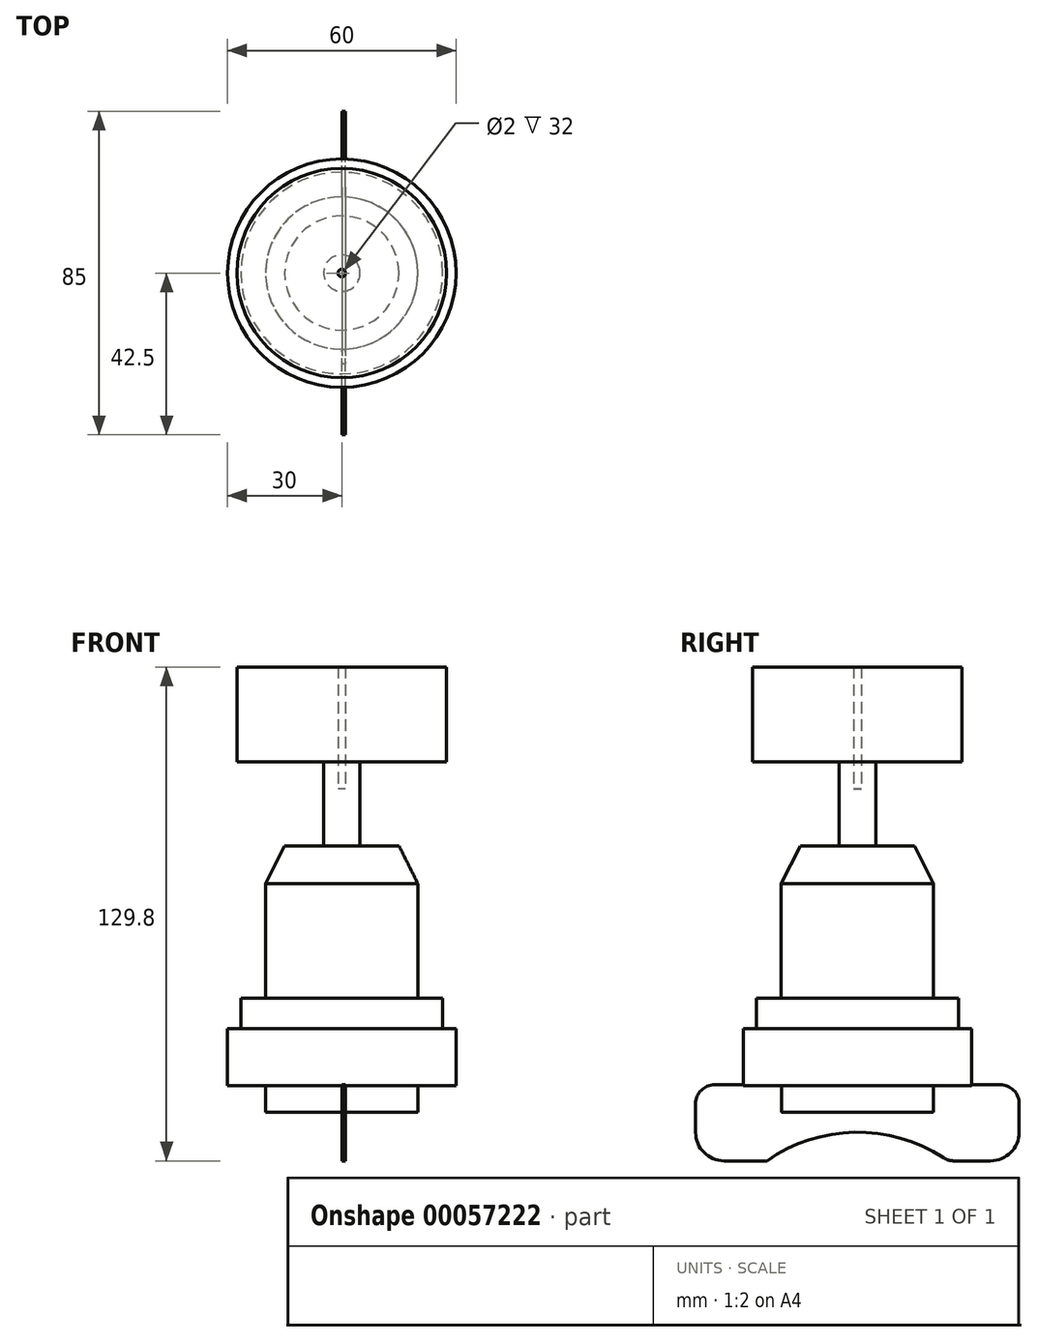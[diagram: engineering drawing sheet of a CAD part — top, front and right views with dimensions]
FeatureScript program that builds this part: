
annotation { "Feature Type Name" : "Feature", "Feature Type Description" : "" }
export const myFeature = defineFeature(function(context is Context, id is Id, definition is map)
    precondition{}
    {
        {
            var Q0;
            Q0=qCreatedBy(makeId("Top.planeOp"),FACE);
            var sketch = newSketch(context, id + "F0", { "sketchPlane" : qUnion([Q0])});
            skCircle(sketch, "E0", {"center": v(0, 0) * mm, "radius": 30 * mm});
            skSolve(sketch);
        }
        {
            var Q0;
            Q0=makeQuery(id+"F0.imprint","IMPRINT",FACE,{"disambiguationData":[TD([[makeQuery(id+"F0.imprint","IMPRINT",EDGE,{"derivedFrom":sQuery(id+"F0.wireOp",EDGE,"E0")}),1.0]])]});
            extrude(context, id + "F1", {"entities" : qUnion([Q0]), "depth" : 15 * mm});
        }
        {
            var Q0;
            Q0=makeQuery(id+"F1.opExtrude","CAP_FACE",FACE,{"disambiguationData":[OSD([sQuery(id+"F0.wireOp",EDGE,"E0")])],"isStart":false});
            var sketch = newSketch(context, id + "F2", { "sketchPlane" : qUnion([Q0])});
            skCircle(sketch, "E1", {"center": v(0, 0) * mm, "radius": 26.5 * mm});
            skSolve(sketch);
        }
        {
            var Q0;
            Q0=makeQuery(id+"F2.imprint","IMPRINT",FACE,{"disambiguationData":[TD([[makeQuery(id+"F2.imprint","IMPRINT",EDGE,{"derivedFrom":sQuery(id+"F2.wireOp",EDGE,"E1")}),1.0]])]});
            var Q1;
            Q1=qSketchRegion(id+"F4",true);
            extrude(context, id + "F3", {"entities" : qUnion([Q0, Q1]), "operationType" : NewBodyOperationType.ADD, "depth" : 8 * mm});
        }
        {
            var Q0;
            Q0=makeQuery(id+"F3.opExtrude","CAP_FACE",FACE,{"disambiguationData":[OSD([sQuery(id+"F2.wireOp",EDGE,"E1")])],"isStart":false});
            var sketch = newSketch(context, id + "F4", { "sketchPlane" : qUnion([Q0])});
            skCircle(sketch, "E2", {"center": v(0, 0) * mm, "radius": 20 * mm});
            skSolve(sketch);
        }
        {
            var Q0;
            Q0=makeQuery(id+"F4.imprint","IMPRINT",FACE,{"disambiguationData":[TD([[makeQuery(id+"F4.imprint","IMPRINT",EDGE,{"derivedFrom":sQuery(id+"F4.wireOp",EDGE,"E2")}),1.0]])]});
            extrude(context, id + "F5", {"entities" : qUnion([Q0]), "operationType" : NewBodyOperationType.ADD, "depth" : 40 * mm});
        }
        {
            var Q0;
            Q0=makeQuery(id+"F1.opExtrude","CAP_FACE",FACE,{"disambiguationData":[OSD([sQuery(id+"F0.wireOp",EDGE,"E0")])],"isStart":true});
            var sketch = newSketch(context, id + "F6", { "sketchPlane" : qUnion([Q0])});
            skCircle(sketch, "E3", {"center": v(0, 0) * mm, "radius": 20 * mm});
            skSolve(sketch);
        }
        {
            var Q0;
            Q0=makeQuery(id+"F6.imprint","IMPRINT",FACE,{"disambiguationData":[TD([[makeQuery(id+"F6.imprint","IMPRINT",EDGE,{"derivedFrom":sQuery(id+"F6.wireOp",EDGE,"E3")}),1.0]])]});
            extrude(context, id + "F7", {"entities" : qUnion([Q0]), "operationType" : NewBodyOperationType.ADD, "depth" : 7 * mm});
        }
        {
            var Q0;
            Q0=qCreatedBy(makeId("Right.planeOp"),FACE);
            var sketch = newSketch(context, id + "F8", { "sketchPlane" : qUnion([Q0])});
            skLineSegment(sketch, "E4.bottom", {"start": v(0, 0.2) * mm, "end": v(-37.5, 0.2) * mm});
            skLineSegment(sketch, "E4.top", {"start": v(0, -19.8) * mm, "end": v(-35, -19.8) * mm});
            skLineSegment(sketch, "E4.left", {"start": v(0, 0.2) * mm, "end": v(0, -19.8) * mm});
            skLineSegment(sketch, "E4.right", {"start": v(-42.5, -4.8) * mm, "end": v(-42.5, -12.3) * mm});
            skLineSegment(sketch, "E5.bottom", {"start": v(0, 0.2) * mm, "end": v(37.5, 0.2) * mm});
            skLineSegment(sketch, "E5.top", {"start": v(0, -19.8) * mm, "end": v(35, -19.8) * mm});
            skLineSegment(sketch, "E5.right", {"start": v(42.5, -4.8) * mm, "end": v(42.5, -12.3) * mm});
            skPoint(sketch, "E6.visualSharp", {"position": v(42.5, -19.8) * mm});
            skArc(sketch, "E6.filletArc", {"start": v(35, -19.8) * mm, "mid": v(40.3, -17.6) * mm, "end": v(42.5, -12.3) * mm});
            skPoint(sketch, "E7.visualSharp", {"position": v(-42.5, -19.8) * mm});
            skArc(sketch, "E7.filletArc", {"start": v(-42.5, -12.3) * mm, "mid": v(-40.3, -17.6) * mm, "end": v(-35, -19.8) * mm});
            skPoint(sketch, "E8.visualSharp", {"position": v(-42.5, 0.2) * mm});
            skArc(sketch, "E8.filletArc", {"start": v(-37.5, 0.2) * mm, "mid": v(-41.04, -1.26) * mm, "end": v(-42.5, -4.8) * mm});
            skPoint(sketch, "E9.visualSharp", {"position": v(42.5, 0.2) * mm});
            skArc(sketch, "E9.filletArc", {"start": v(42.5, -4.8) * mm, "mid": v(41.04, -1.26) * mm, "end": v(37.5, 0.2) * mm});
            skSolve(sketch);
        }
        {
            var Q0;
            Q0=makeQuery(id+"F8.imprint","IMPRINT",FACE,{"disambiguationData":[TD([[makeQuery(id+"F8.imprint","IMPRINT",EDGE,{"derivedFrom":sQuery(id+"F8.wireOp",EDGE,"E5.bottom")}),-1.0]])]});
            var Q1;
            Q1=makeQuery(id+"F8.imprint","IMPRINT",FACE,{"disambiguationData":[TD([[makeQuery(id+"F8.imprint","IMPRINT",EDGE,{"derivedFrom":sQuery(id+"F8.wireOp",EDGE,"E4.bottom")}),1.0]])]});
            extrude(context, id + "F9", {"entities" : qUnion([Q0, Q1]), "operationType" : NewBodyOperationType.ADD, "depth" : 1 * mm});
        }
        {
            var Q0;
            Q0=makeQuery(id+"F9.opExtrude","CAP_FACE",FACE,{"disambiguationData":[OSD([sQuery(id+"F8.wireOp",EDGE,"E4.bottom"),sQuery(id+"F8.wireOp",EDGE,"E4.top"),sQuery(id+"F8.wireOp",EDGE,"E4.right"),sQuery(id+"F8.wireOp",EDGE,"E5.bottom"),sQuery(id+"F8.wireOp",EDGE,"E5.top"),sQuery(id+"F8.wireOp",EDGE,"E5.right"),sQuery(id+"F8.wireOp",EDGE,"E6.filletArc"),sQuery(id+"F8.wireOp",EDGE,"E7.filletArc"),sQuery(id+"F8.wireOp",EDGE,"E8.filletArc"),sQuery(id+"F8.wireOp",EDGE,"E9.filletArc")])],"isStart":false});
            var sketch = newSketch(context, id + "F10", { "sketchPlane" : qUnion([Q0])});
            skCircle(sketch, "E10", {"center": v(0, -53.67) * mm, "radius": 41.39 * mm});
            skSolve(sketch);
        }
        {
            var Q0;
            {var subQ0=makeQuery(id+"F9.opExtrude","CAP_EDGE",EDGE,{"disambiguationData":[OSD([sQuery(id+"F8.wireOp",EDGE,"E4.top"),sQuery(id+"F8.wireOp",EDGE,"E5.top")])],"isStart":false});var subQ1=sQuery(id+"F10.wireOp",EDGE,"E10");var subQ3=makeQuery(id+"F10.imprint","INTERSECT",VERTEX,{"disambiguationData":[OD(0.0)],"derivedFrom":[subQ0,subQ1]});Q0=makeQuery(id+"F10.imprint","IMPRINT",FACE,{"disambiguationData":[TD([[makeQuery(id+"F10.imprint","IMPRINT",EDGE,{"disambiguationData":[TD([[subQ3,1.0]])],"derivedFrom":subQ1}),1.0]])]});}
            extrude(context, id + "F11", {"entities" : qUnion([Q0]), "operationType" : NewBodyOperationType.REMOVE, "oppositeDirection" : true, "depth" : 25 * mm});
        }
        {
            var Q0;
            {var subQ0=sQuery(id+"F8.wireOp",EDGE,"E4.top");var subQ1=sQuery(id+"F8.wireOp",EDGE,"E5.top");var subQ2=sQuery(id+"F10.wireOp",EDGE,"E10");Q0=makeQuery(id+"F11.boolean.opBoolean","COPY",EDGE,{"derivedFrom":makeQuery(id+"F11.opExtrude","SWEPT_EDGE",EDGE,{"disambiguationData":[OSD([subQ0,subQ1,subQ2]),TDD([makeQuery(id+"F10.imprint","INTERSECT",VERTEX,{"disambiguationData":[OD(0.0)],"derivedFrom":[makeQuery(id+"F9.opExtrude","CAP_EDGE",EDGE,{"disambiguationData":[OSD([subQ0,subQ1])],"isStart":false}),subQ2]})])]})});}
            var Q1;
            {var subQ0=sQuery(id+"F8.wireOp",EDGE,"E4.top");var subQ1=sQuery(id+"F8.wireOp",EDGE,"E5.top");var subQ2=sQuery(id+"F10.wireOp",EDGE,"E10");Q1=makeQuery(id+"F11.boolean.opBoolean","COPY",EDGE,{"derivedFrom":makeQuery(id+"F11.opExtrude","SWEPT_EDGE",EDGE,{"disambiguationData":[OSD([subQ0,subQ1,subQ2]),TDD([makeQuery(id+"F10.imprint","INTERSECT",VERTEX,{"disambiguationData":[OD(1.0)],"derivedFrom":[makeQuery(id+"F9.opExtrude","CAP_EDGE",EDGE,{"disambiguationData":[OSD([subQ0,subQ1])],"isStart":false}),subQ2]})])]})});}
            fillet(context, id + "F12", {"entities" : qUnion([Q0, Q1]), "radius" : 5 * mm, "tangentPropagation" : true, "allowEdgeOverflow" : false});
        }
        {
            var Q0;
            Q0=makeQuery(id+"F5.opExtrude","CAP_EDGE",EDGE,{"disambiguationData":[OSD([sQuery(id+"F4.wireOp",EDGE,"E2")])],"isStart":false});
            chamfer(context, id + "F13", {"entities" : qUnion([Q0]), "chamferType" : ChamferType.TWO_OFFSETS, "width1" : 5 * mm, "oppositeDirection" : false, "width2" : 10 * mm, "tangentPropagation" : true});
        }
        {
            var Q0;
            Q0=makeQuery(id+"F5.opExtrude","CAP_FACE",FACE,{"disambiguationData":[OSD([sQuery(id+"F4.wireOp",EDGE,"E2")])],"isStart":false});
            var sketch = newSketch(context, id + "F14", { "sketchPlane" : qUnion([Q0])});
            skCircle(sketch, "E11", {"center": v(0, 0) * mm, "radius": 1 * mm});
            skSolve(sketch);
        }
        {
            var Q0;
            Q0=qSketchRegion(id+"F14",true);
            extrude(context, id + "F15", {"entities" : qUnion([Q0]), "operationType" : NewBodyOperationType.ADD, "depth" : 15 * mm});
        }
        {
            var Q0;
            Q0=makeQuery(id+"F5.opExtrude","CAP_FACE",FACE,{"disambiguationData":[OSD([sQuery(id+"F4.wireOp",EDGE,"E2")])],"isStart":false});
            var sketch = newSketch(context, id + "F16", { "sketchPlane" : qUnion([Q0])});
            skCircle(sketch, "E12", {"center": v(0, 0) * mm, "radius": 4.8 * mm});
            skSolve(sketch);
        }
        {
            var Q0;
            Q0=makeQuery(id+"F16.imprint","IMPRINT",FACE,{"disambiguationData":[TD([[makeQuery(id+"F16.imprint","IMPRINT",EDGE,{"derivedFrom":makeQuery(id+"F15.opExtrude","CAP_EDGE",EDGE,{"disambiguationData":[OSD([sQuery(id+"F14.wireOp",EDGE,"E11")])],"isStart":true})}),1.0]])]});
            var Q1;
            Q1=makeQuery(id+"F16.imprint","IMPRINT",FACE,{"disambiguationData":[TD([[makeQuery(id+"F16.imprint","IMPRINT",EDGE,{"derivedFrom":sQuery(id+"F16.wireOp",EDGE,"E12")}),1.0]])]});
            extrude(context, id + "F17", {"entities" : qUnion([Q0, Q1]), "operationType" : NewBodyOperationType.ADD, "depth" : 22 * mm});
        }
        {
            var Q0;
            Q0=makeQuery(id+"F17.opExtrude","CAP_FACE",FACE,{"disambiguationData":[OSD([sQuery(id+"F16.wireOp",EDGE,"E12")])],"isStart":false});
            var sketch = newSketch(context, id + "F18", { "sketchPlane" : qUnion([Q0])});
            skCircle(sketch, "E13", {"center": v(0, 0) * mm, "radius": 27.5 * mm});
            skSolve(sketch);
        }
        {
            var Q0;
            Q0=makeQuery(id+"F18.imprint","IMPRINT",FACE,{"disambiguationData":[TD([[makeQuery(id+"F18.imprint","IMPRINT",EDGE,{"derivedFrom":sQuery(id+"F18.wireOp",EDGE,"E13")}),1.0]])]});
            var Q1;
            Q1=makeQuery(id+"F18.imprint","IMPRINT",FACE,{"disambiguationData":[TD([[makeQuery(id+"F18.imprint","IMPRINT",EDGE,{"derivedFrom":makeQuery(id+"F17.opExtrude","CAP_EDGE",EDGE,{"disambiguationData":[OSD([sQuery(id+"F16.wireOp",EDGE,"E12")])],"isStart":false})}),1.0]])]});
            extrude(context, id + "F19", {"entities" : qUnion([Q0, Q1]), "operationType" : NewBodyOperationType.ADD, "depth" : 25 * mm});
        }
    });
